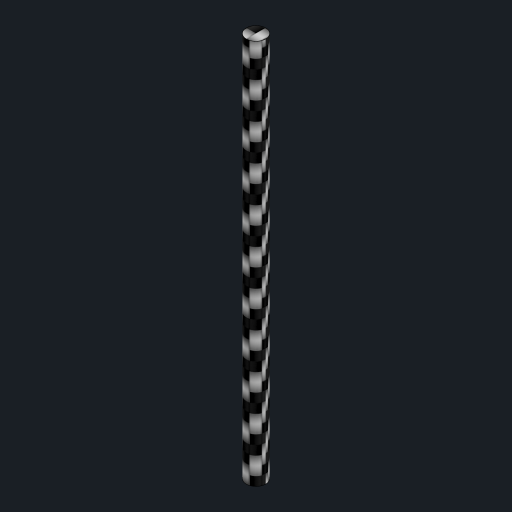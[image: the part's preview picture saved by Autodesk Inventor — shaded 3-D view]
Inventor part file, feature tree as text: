
AUTODESK INVENTOR PART (.ipt)
format: ipt  version: 2023 (Build 270158000, 158)  size: 102,400 bytes
history: native  units: mm
features: other x1, extrude x1, sketch x1
ambient origin geometry x8: Origin, YZ Plane, XZ Plane, XY Plane, X Axis, Y Axis, Z Axis, Center Point
bodies: Body1 (feature_tree)
feature tree (3):
  other  "ソリッド1"
  extrude  "押し出し1"  Depth=2.0mm
  sketch  "スケッチ1"
